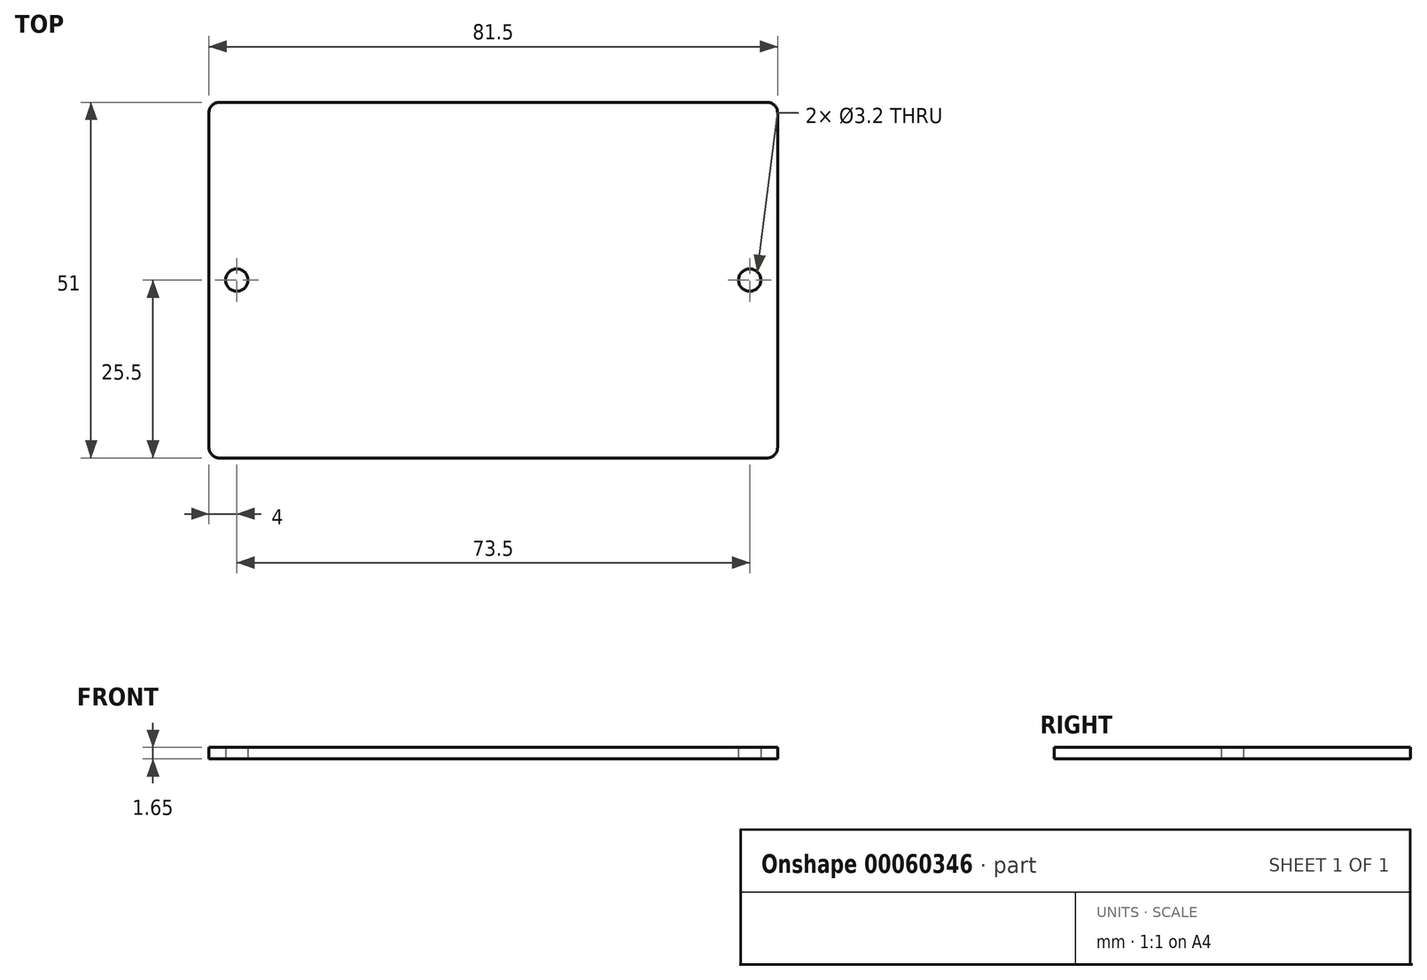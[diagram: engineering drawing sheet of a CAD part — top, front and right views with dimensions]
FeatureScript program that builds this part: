
annotation { "Feature Type Name" : "Feature", "Feature Type Description" : "" }
export const myFeature = defineFeature(function(context is Context, id is Id, definition is map)
    precondition{}
    {
        {
            var Q0;
            Q0=qCreatedBy(makeId("Top.planeOp"),FACE);
            var sketch = newSketch(context, id + "F0", { "sketchPlane" : qUnion([Q0])});
            skLineSegment(sketch, "E0.bottom", {"start": v(-39.25, 25.5) * mm, "end": v(39.25, 25.5) * mm});
            skLineSegment(sketch, "E0.top", {"start": v(-39.25, -25.5) * mm, "end": v(39.25, -25.5) * mm});
            skLineSegment(sketch, "E0.left", {"start": v(-40.75, 24) * mm, "end": v(-40.75, -24) * mm});
            skLineSegment(sketch, "E0.right", {"start": v(40.75, 24) * mm, "end": v(40.75, -24) * mm});
            skCircle(sketch, "E1", {"center": v(-36.75, 0) * mm, "radius": 1.6 * mm});
            skCircle(sketch, "E2", {"center": v(36.75, 0) * mm, "radius": 1.6 * mm});
            skPoint(sketch, "E3.visualSharp", {"position": v(-40.75, 25.5) * mm});
            skArc(sketch, "E3.filletArc", {"start": v(-39.25, 25.5) * mm, "mid": v(-40.31, 25.06) * mm, "end": v(-40.75, 24) * mm});
            skPoint(sketch, "E4.visualSharp", {"position": v(40.75, 25.5) * mm});
            skArc(sketch, "E4.filletArc", {"start": v(40.75, 24) * mm, "mid": v(40.31, 25.06) * mm, "end": v(39.25, 25.5) * mm});
            skPoint(sketch, "E5.visualSharp", {"position": v(40.75, -25.5) * mm});
            skArc(sketch, "E5.filletArc", {"start": v(39.25, -25.5) * mm, "mid": v(40.31, -25.06) * mm, "end": v(40.75, -24) * mm});
            skPoint(sketch, "E6.visualSharp", {"position": v(-40.75, -25.5) * mm});
            skArc(sketch, "E6.filletArc", {"start": v(-40.75, -24) * mm, "mid": v(-40.31, -25.06) * mm, "end": v(-39.25, -25.5) * mm});
            skSolve(sketch);
        }
        {
            var Q0;
            Q0 = qSketchRegion(id + "F0", true);
            extrude(context, id + "F1", {"entities" : qUnion([Q0]), "depth" : 1.65 * mm});
        }
    });
